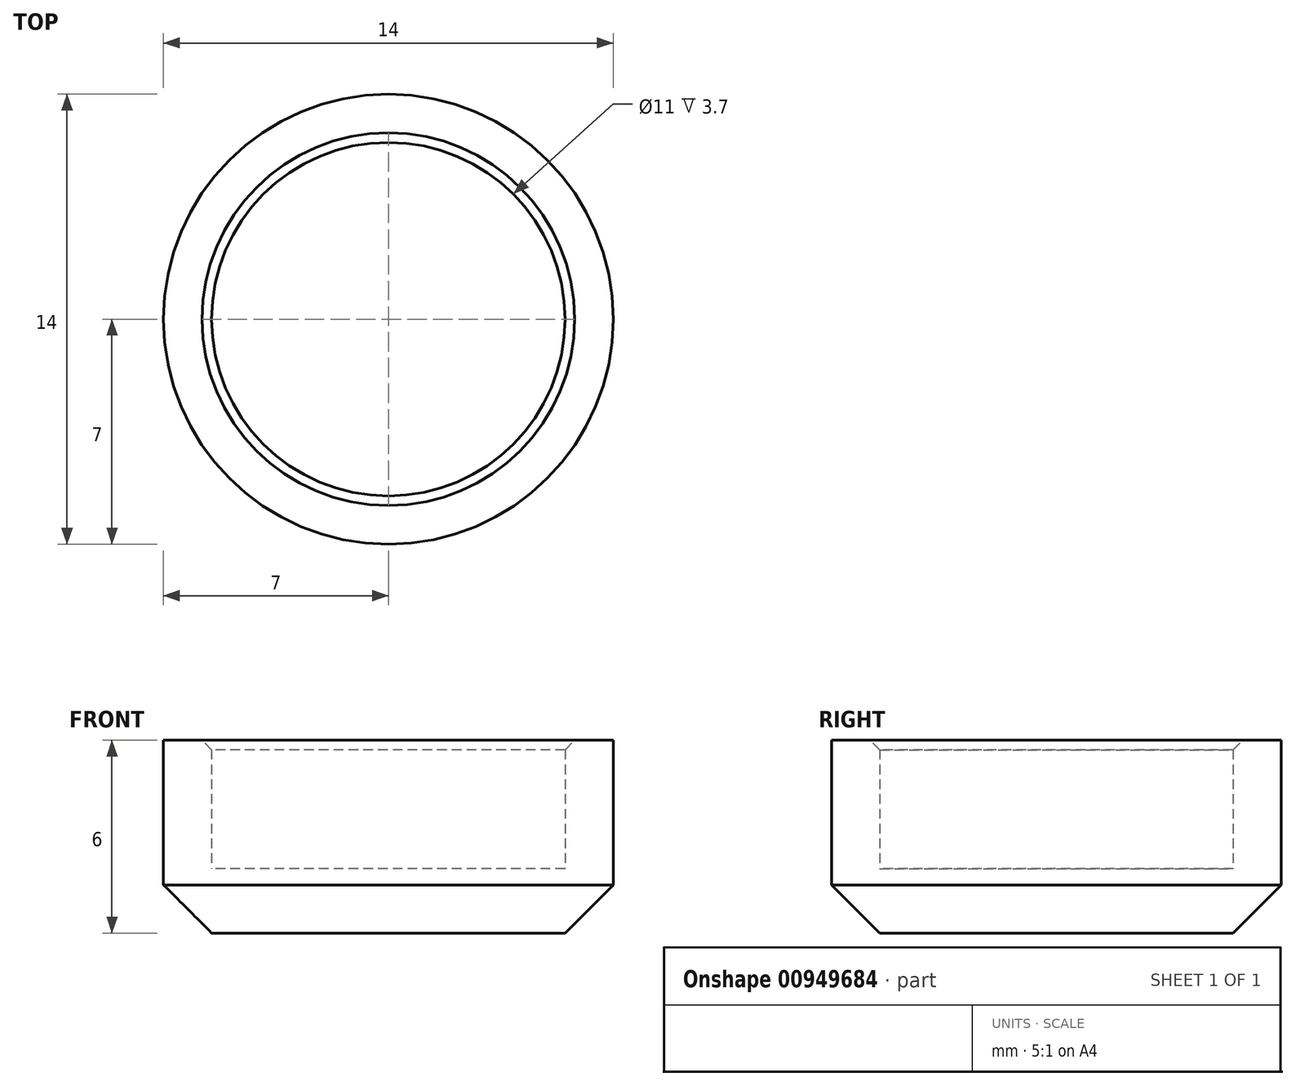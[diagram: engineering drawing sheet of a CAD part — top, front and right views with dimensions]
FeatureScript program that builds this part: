
annotation { "Feature Type Name" : "Feature", "Feature Type Description" : "" }
export const myFeature = defineFeature(function(context is Context, id is Id, definition is map)
    precondition{}
    {
        {
            var Q0;
            Q0=qCreatedBy(makeId("Top.planeOp"),FACE);
            var sketch = newSketch(context, id + "F0", { "sketchPlane" : qUnion([Q0])});
            skCircle(sketch, "E0", {"center": v(0, 0) * mm, "radius": 5.5 * mm});
            skCircle(sketch, "E1", {"center": v(0, 0) * mm, "radius": 7 * mm});
            skSolve(sketch);
        }
        {
            var Q0;
            Q0=makeQuery(id+"F0.imprint","IMPRINT",FACE,{"disambiguationData":[TD([[makeQuery(id+"F0.imprint","IMPRINT",EDGE,{"derivedFrom":sQuery(id+"F0.wireOp",EDGE,"E0")}),-1.0]])]});
            extrude(context, id + "F1", {"entities" : qUnion([Q0]), "depth" : 4 * mm, "offsetDistance" : 25 * mm});
        }
        {
            var Q0;
            Q0=makeQuery(id+"F1.opExtrude","CAP_FACE",FACE,{"disambiguationData":[OSD([sQuery(id+"F0.wireOp",EDGE,"E0"),sQuery(id+"F0.wireOp",EDGE,"E1")])],"isStart":true});
            var sketch = newSketch(context, id + "F2", { "sketchPlane" : qUnion([Q0])});
            skCircle(sketch, "E2.0", {"center": v(0, 0) * mm, "radius": 7 * mm});
            skSolve(sketch);
        }
        {
            var Q0;
            Q0 = qSketchRegion(id + "F2", true);
            extrude(context, id + "F3", {"entities" : qUnion([Q0]), "operationType" : NewBodyOperationType.ADD, "depth" : 2 * mm, "offsetDistance" : 25 * mm});
        }
        {
            var Q0;
            Q0=makeQuery(id+"F3.opExtrude","CAP_EDGE",EDGE,{"disambiguationData":[OSD([sQuery(id+"F2.wireOp",EDGE,"E2.0")])],"isStart":false});
            chamfer(context, id + "F4", {"entities" : qUnion([Q0]), "width" : 1.5 * mm, "tangentPropagation" : true});
        }
        {
            var Q0;
            Q0=makeQuery(id+"F1.opExtrude","CAP_EDGE",EDGE,{"disambiguationData":[OSD([sQuery(id+"F0.wireOp",EDGE,"E0")])],"isStart":false});
            chamfer(context, id + "F5", {"entities" : qUnion([Q0]), "width" : 0.3 * mm, "tangentPropagation" : true});
        }
    });
